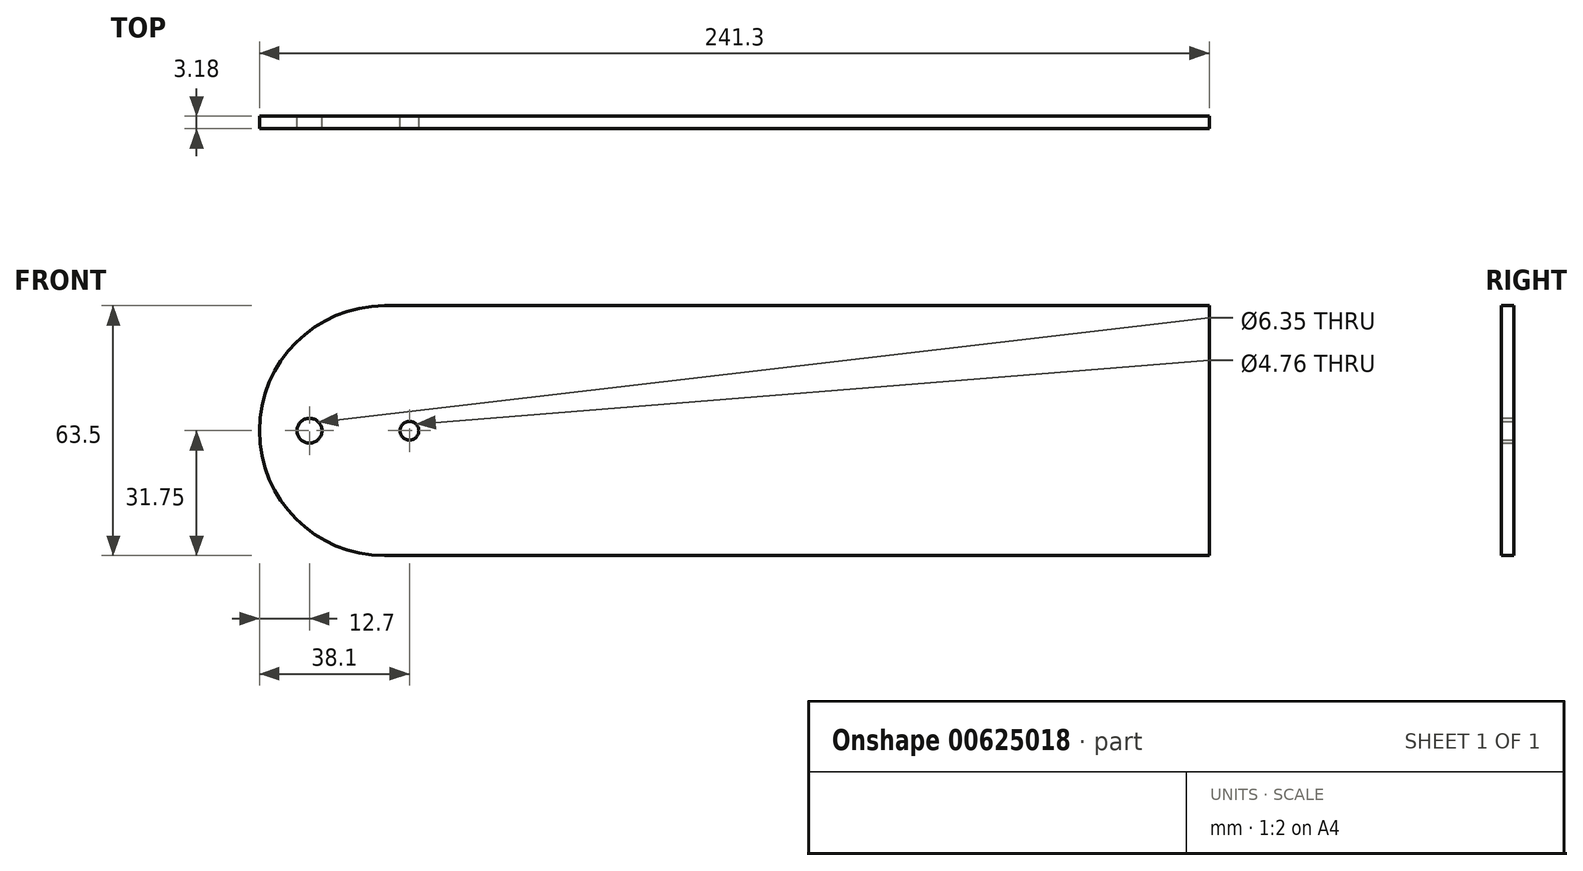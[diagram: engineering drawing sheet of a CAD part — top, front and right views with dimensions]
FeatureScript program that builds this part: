
annotation { "Feature Type Name" : "Feature", "Feature Type Description" : "" }
export const myFeature = defineFeature(function(context is Context, id is Id, definition is map)
    precondition{}
    {
        {
            var Q0;
            Q0=qCreatedBy(makeId("Front.planeOp"),FACE);
            var sketch = newSketch(context, id + "F0", { "sketchPlane" : qUnion([Q0])});
            skLineSegment(sketch, "E0.bottom", {"start": v(31.75, 0) * mm, "end": v(241.3, 0) * mm});
            skLineSegment(sketch, "E0.top", {"start": v(31.75, 63.5) * mm, "end": v(241.3, 63.5) * mm});
            skLineSegment(sketch, "E0.left", {"start": v(0, 31.75) * mm, "end": v(0, 31.75) * mm});
            skLineSegment(sketch, "E1", {"start": v(0, 31.75) * mm, "end": v(38.1, 31.75) * mm});
            skPoint(sketch, "E1.endSnap0", {"position": v(0, 31.75) * mm});
            skCircle(sketch, "E2", {"center": v(38.1, 31.75) * mm, "radius": 2.38 * mm});
            skCircle(sketch, "E3", {"center": v(38.1, 31.75) * mm, "radius": 25.4 * mm});
            skLineSegment(sketch, "E4", {"start": v(12.7, 31.75) * mm, "end": v(38.1, 31.75) * mm});
            skPoint(sketch, "E5.visualSharp", {"position": v(0, 63.5) * mm});
            skArc(sketch, "E5.filletArc", {"start": v(31.75, 63.5) * mm, "mid": v(9.3, 54.2) * mm, "end": v(0, 31.75) * mm});
            skPoint(sketch, "E6.visualSharp", {"position": v(0, 0) * mm});
            skArc(sketch, "E6.filletArc", {"start": v(0, 31.75) * mm, "mid": v(9.3, 9.3) * mm, "end": v(31.75, 0) * mm});
            skCircle(sketch, "E7", {"center": v(12.7, 31.75) * mm, "radius": 3.18 * mm});
            skLineSegment(sketch, "E8", {"start": v(241.3, 63.5) * mm, "end": v(241.3, 0) * mm});
            skSolve(sketch);
        }
        {
            var Q0;
            {var subQ0=sQuery(id+"F0.wireOp",EDGE,"O3syXbHt-yHTN-aNau-WEg2-3ZSHqx7OYMuC");var subQ3=sQuery(id+"F0.wireOp",EDGE,"E0.top");var subQ4=makeQuery(id+"F0.imprint","INTERSECT",VERTEX,{"disambiguationData":[OD(0.0)],"derivedFrom":[subQ3,subQ0]});Q0=makeQuery(id+"F0.imprint","IMPRINT",FACE,{"disambiguationData":[TD([[makeQuery(id+"F0.imprint","IMPRINT",EDGE,{"disambiguationData":[TD([[subQ4,-1.0]])],"derivedFrom":subQ3}),-1.0]])]});}
            var Q1;
            {var subQ1=sQuery(id+"F0.wireOp",EDGE,"E0.bottom");var subQ5=sQuery(id+"F0.wireOp",EDGE,"O3syXbHt-yHTN-aNau-WEg2-3ZSHqx7OYMuC");var subQ8=makeQuery(id+"F0.imprint","INTERSECT",VERTEX,{"disambiguationData":[OD(0.0)],"derivedFrom":[subQ1,subQ5]});Q1=makeQuery(id+"F0.imprint","IMPRINT",FACE,{"disambiguationData":[TD([[makeQuery(id+"F0.imprint","IMPRINT",EDGE,{"disambiguationData":[TD([[subQ8,-1.0]])],"derivedFrom":subQ1}),1.0]])]});}
            var Q2;
            Q2=makeQuery(id+"F0.imprint","IMPRINT",FACE,{"disambiguationData":[TD([[makeQuery(id+"F0.imprint","IMPRINT",EDGE,{"derivedFrom":sQuery(id+"F0.wireOp",EDGE,"E2")}),-1.0]])]});
            var Q3;
            {var subQ0=sQuery(id+"F0.wireOp",EDGE,"O3syXbHt-yHTN-aNau-WEg2-3ZSHqx7OYMuC");var subQ1=sQuery(id+"F0.wireOp",EDGE,"E0.bottom");var subQ2=makeQuery(id+"F0.imprint","INTERSECT",VERTEX,{"disambiguationData":[OD(1.0)],"derivedFrom":[subQ1,subQ0]});Q3=makeQuery(id+"F0.imprint","IMPRINT",FACE,{"disambiguationData":[TD([[makeQuery(id+"F0.imprint","IMPRINT",EDGE,{"disambiguationData":[TD([[subQ2,1.0]])],"derivedFrom":subQ1}),1.0]])]});}
            var Q4;
            {var subQ0=sQuery(id+"F0.wireOp",EDGE,"O3syXbHt-yHTN-aNau-WEg2-3ZSHqx7OYMuC");var subQ1=sQuery(id+"F0.wireOp",EDGE,"E0.bottom");var subQ2=makeQuery(id+"F0.imprint","INTERSECT",VERTEX,{"disambiguationData":[OD(1.0)],"derivedFrom":[subQ1,subQ0]});Q4=makeQuery(id+"F0.imprint","IMPRINT",FACE,{"disambiguationData":[TD([[makeQuery(id+"F0.imprint","IMPRINT",EDGE,{"disambiguationData":[TD([[subQ2,-1.0]])],"derivedFrom":subQ1}),1.0]])]});}
            var Q5;
            {var subQ5=sQuery(id+"F0.wireOp",EDGE,"E0.right");Q5=makeQuery(id+"F0.imprint","IMPRINT",FACE,{"disambiguationData":[TD([[makeQuery(id+"F0.imprint","IMPRINT",EDGE,{"derivedFrom":subQ5}),1.0]])]});}
            var Q6;
            {var subQ0=sQuery(id+"F0.wireOp",EDGE,"3Y4z7vdy-5k93-72MP-tSkG-mfVYHQxSRFQm");var subQ1=sQuery(id+"F0.wireOp",EDGE,"HRHAH4qI-ovDE-Goyb-KF3L-RjTyW2WzQh8t");var subQ2=makeQuery(id+"F0.imprint","INTERSECT",VERTEX,{"disambiguationData":[OD(0.0)],"derivedFrom":[subQ1,subQ0]});Q6=makeQuery(id+"F0.imprint","IMPRINT",FACE,{"disambiguationData":[TD([[makeQuery(id+"F0.imprint","IMPRINT",EDGE,{"disambiguationData":[TD([[subQ2,-1.0]])],"derivedFrom":subQ1}),1.0]])]});}
            var Q7;
            {var subQ0=sQuery(id+"F0.wireOp",EDGE,"3Y4z7vdy-5k93-72MP-tSkG-mfVYHQxSRFQm");var subQ1=sQuery(id+"F0.wireOp",EDGE,"HRHAH4qI-ovDE-Goyb-KF3L-RjTyW2WzQh8t");var subQ2=makeQuery(id+"F0.imprint","INTERSECT",VERTEX,{"disambiguationData":[OD(0.0)],"derivedFrom":[subQ1,subQ0]});Q7=makeQuery(id+"F0.imprint","IMPRINT",FACE,{"disambiguationData":[TD([[makeQuery(id+"F0.imprint","IMPRINT",EDGE,{"disambiguationData":[TD([[subQ2,-1.0]])],"derivedFrom":subQ1}),-1.0]])]});}
            var Q8;
            {var subQ11=sQuery(id+"F0.wireOp",EDGE,"E5.filletArc");Q8=makeQuery(id+"F0.imprint","IMPRINT",FACE,{"disambiguationData":[TD([[makeQuery(id+"F0.imprint","IMPRINT",EDGE,{"derivedFrom":subQ11}),1.0]])]});}
            extrude(context, id + "F1", {"entities" : qUnion([Q0, Q1, Q2, Q3, Q4, Q5, Q6, Q7, Q8]), "depth" : 3.17 * mm, "offsetDistance" : 25.4 * mm});
        }
    });
